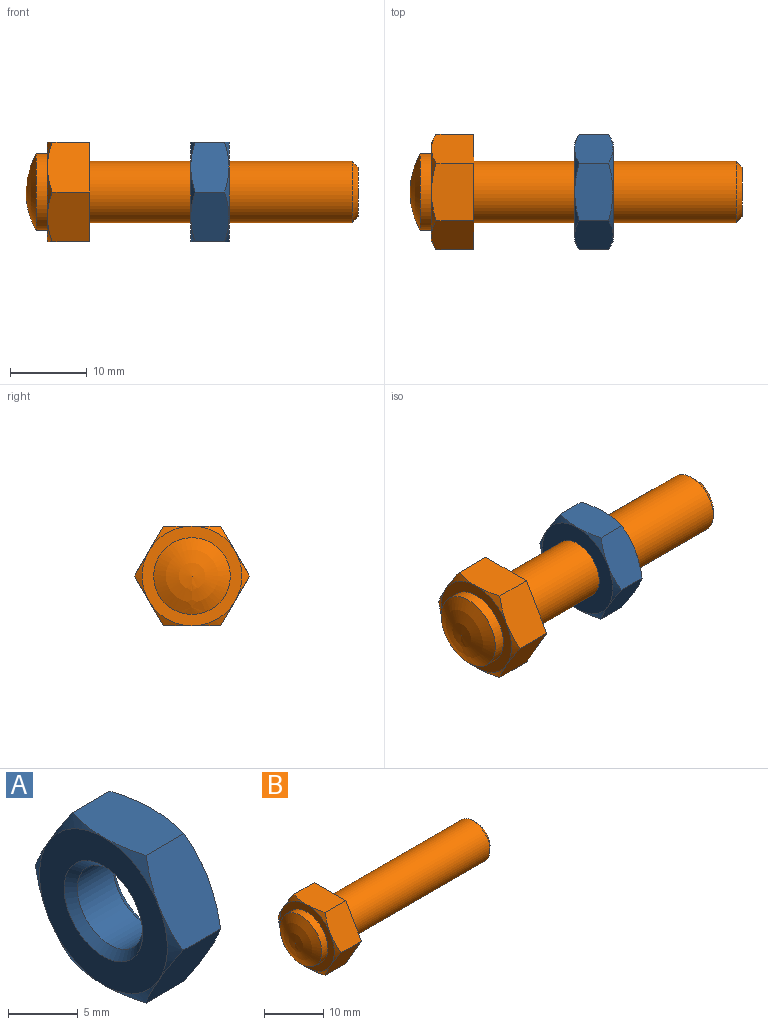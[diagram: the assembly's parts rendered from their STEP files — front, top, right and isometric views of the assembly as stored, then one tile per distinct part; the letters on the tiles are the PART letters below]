
ASSEMBLY  parts=2 mates=1
PART A: 23 faces, bbox 5x15x15 mm
  f0: cone r=7.8mm half-angle=60deg, axis (-1,0,0), area 2.6mm2, adj f4,f6,f14
  f1: plane 6.5x5mm, normal (0,0.87,0.5), area 34.5mm2, adj f2,f8,f10,f15,f16,f22
  f2: plane 6.5x5mm, normal (0,0.87,-0.5), area 34.5mm2, adj f1,f3,f5,f13,f15,f22
  f3: plane 7.51x5mm, normal (0,0,-1), area 34.5mm2, adj f2,f5,f6,f12,f13,f18
  f4: plane 6.5x5mm, normal (0,-0.87,0.5), area 34.5mm2, adj f0,f6,f7,f9,f10,f17
  f5: cone r=7.8mm half-angle=60deg, axis (-1,0,0), area 2.6mm2, adj f2,f3,f14
  f6: plane 6.5x5mm, normal (0,-0.87,-0.5), area 34.5mm2, adj f0,f3,f4,f9,f12,f18
  f7: cone r=6.5mm half-angle=60deg, axis (1,0,0), area 2.6mm2, adj f4,f10,f11
  f8: cone r=6.5mm half-angle=60deg, axis (1,0,0), area 2.6mm2, adj f1,f10,f11
  f9: cone r=6.5mm half-angle=60deg, axis (1,0,0), area 2.6mm2, adj f4,f6,f11
  f10: plane 7.51x5mm, normal (0,0,1), area 34.5mm2, adj f1,f4,f7,f8,f16,f17
  f11: plane 13x13mm, normal (-1,0,0), area 82.5mm2, adj f7,f8,f9,f12,f13,f19,f22
  f12: cone r=6.5mm half-angle=60deg, axis (1,0,0), area 2.6mm2, adj f3,f6,f11
  f13: cone r=6.5mm half-angle=60deg, axis (1,0,0), area 2.6mm2, adj f2,f3,f11
  f14: plane 13x13mm, normal (1,0,0), area 82.5mm2, adj f0,f5,f15,f16,f17,f18,f21
  f15: cone r=7.8mm half-angle=60deg, axis (-1,0,0), area 2.6mm2, adj f1,f2,f14
  f16: cone r=7.8mm half-angle=60deg, axis (-1,0,0), area 2.6mm2, adj f1,f10,f14
  f17: cone r=7.8mm half-angle=60deg, axis (-1,0,0), area 2.6mm2, adj f4,f10,f14
  f18: cone r=7.8mm half-angle=60deg, axis (-1,0,0), area 2.6mm2, adj f3,f6,f14
  f19: cone r=4mm half-angle=45deg, axis (-1,0,0), area 22mm2, adj f11,f20
  f20: cylinder r=3.32mm len=6.65mm, axis (-1,0,0), area 76.2mm2, adj f19,f21
  f21: cone r=3.32mm half-angle=45deg, axis (1,0,0), area 22mm2, adj f14,f20
  f22: cone r=6.5mm half-angle=60deg, axis (1,0,0), area 2.6mm2, adj f1,f2,f11
PART B: 19 faces, bbox 43.3x15x15 mm
  f0: plane 6.5x5.5mm, normal (0,-0.87,0.5), area 39.8mm2, adj f4,f7,f9,f15,f18
  f1: plane 6.47x6.47mm, normal (1,0,0), area 32.8mm2, adj f2
  f2: cone r=4mm half-angle=45deg, axis (-1,0,0), area 24.6mm2, adj f1,f3
  f3: cylinder r=4mm len=34.23mm, axis (-1,0,0), area 860.4mm2, adj f2,f4
  f4: plane 15.01x13mm, normal (1,0,0), area 96.1mm2, adj f0,f3,f10,f11,f12,f15,f18
  f5: cone r=6.5mm half-angle=60deg, axis (1,0,0), area 2.6mm2, adj f10,f11,f14
  f6: cone r=6.5mm half-angle=60deg, axis (1,0,0), area 2.6mm2, adj f11,f12,f14
  f7: cone r=6.5mm half-angle=60deg, axis (1,0,0), area 2.6mm2, adj f0,f14,f18
  f8: sphere r=10mm, area 84.2mm2, adj f13
  f9: cone r=6.5mm half-angle=60deg, axis (1,0,0), area 2.6mm2, adj f0,f14,f15
  f10: plane 7.51x5.5mm, normal (0,0,-1), area 39.8mm2, adj f4,f5,f11,f17,f18
  f11: plane 6.5x5.5mm, normal (0,0.87,-0.5), area 39.8mm2, adj f4,f5,f6,f10,f12
  f12: plane 6.5x5.5mm, normal (0,0.87,0.5), area 39.8mm2, adj f4,f6,f11,f15,f16
  f13: cylinder r=5mm len=10mm, axis (-1,0,0), area 45.9mm2, adj f8,f14
  f14: plane 13x13mm, normal (-1,0,0), area 54.2mm2, adj f5,f6,f7,f9,f13,f16,f17
  f15: plane 7.51x5.5mm, normal (0,0,1), area 39.8mm2, adj f0,f4,f9,f12,f16
  f16: cone r=6.5mm half-angle=60deg, axis (1,0,0), area 2.6mm2, adj f12,f14,f15
  f17: cone r=6.5mm half-angle=60deg, axis (1,0,0), area 2.6mm2, adj f10,f14,f18
  f18: plane 6.5x5.5mm, normal (0,-0.87,-0.5), area 39.8mm2, adj f0,f4,f7,f10,f17
PLACE A rot(axis=(0,0,1),180deg) t=(15.68,-22.67,1.64)mm
PLACE B t=(0,-22.67,1.64)mm
MATE cylindrical A.f0 <-> B.f2  axis (1,0,0) through (17.5,-22.67,1.64)mm
